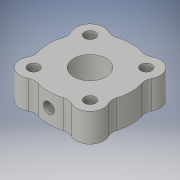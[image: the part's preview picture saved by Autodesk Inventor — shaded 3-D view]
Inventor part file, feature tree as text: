
AUTODESK INVENTOR PART (.ipt)
format: ipt  version: 2016 (Build 200138000, 138)  size: 155,648 bytes
history: native  units: in
note: dims shown in document units (in); Inventor stores cm internally (conversion verified against a paired STEP export)
features: fillet x1
ambient origin geometry x8: Origin, YZ Plane, XZ Plane, XY Plane, X Axis, Y Axis, Z Axis, Center Point
bodies: Solid1 (feature_tree)
feature tree (1):
  fillet  "Fillet1"  [1 undecoded]
note: 1 required parameter value undecoded (feature->parameter linkage not recoverable at this tier; creation-order binding heuristic only, values carry confidence <= 0.55)
